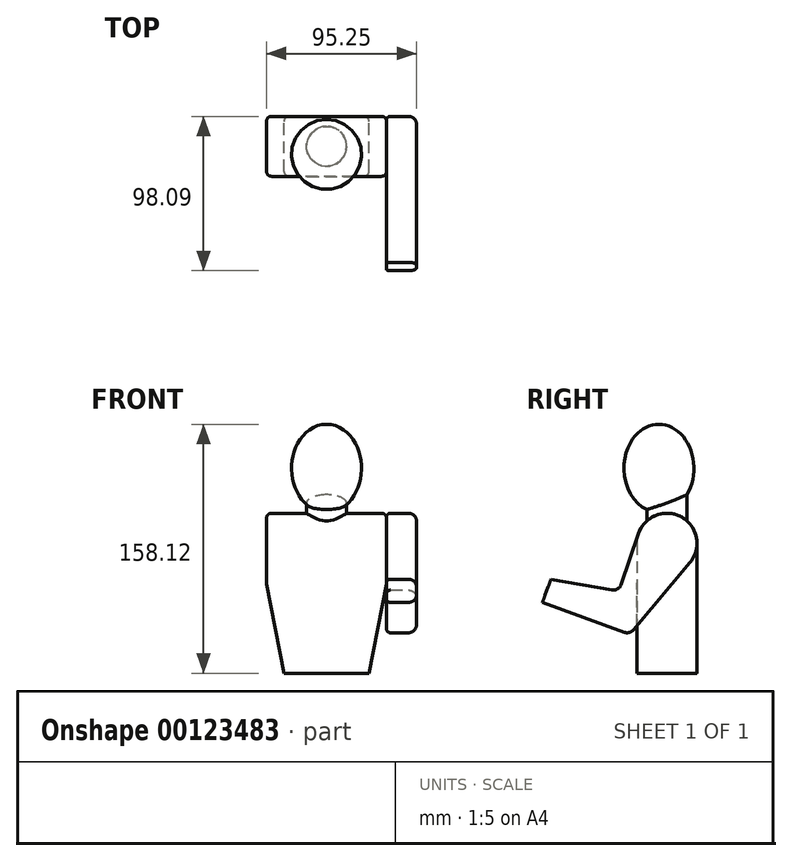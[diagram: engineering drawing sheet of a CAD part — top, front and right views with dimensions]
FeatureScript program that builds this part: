
annotation { "Feature Type Name" : "Feature", "Feature Type Description" : "" }
export const myFeature = defineFeature(function(context is Context, id is Id, definition is map)
    precondition{}
    {
        {
            var Q0;
            Q0=qCreatedBy(makeId("Front.planeOp"),FACE);
            var sketch = newSketch(context, id + "F0", { "sketchPlane" : qUnion([Q0])});
            skLineSegment(sketch, "E0", {"start": v(-26.99, 0) * mm, "end": v(26.99, 0) * mm});
            skLineSegment(sketch, "E1", {"start": v(26.99, 0) * mm, "end": v(38.1, 57.15) * mm});
            skLineSegment(sketch, "E2", {"start": v(38.1, 57.15) * mm, "end": v(38.1, 101.6) * mm});
            skLineSegment(sketch, "E3", {"start": v(38.1, 101.6) * mm, "end": v(-38.1, 101.6) * mm});
            skLineSegment(sketch, "E4", {"start": v(-38.1, 101.6) * mm, "end": v(-38.1, 57.15) * mm});
            skLineSegment(sketch, "E5", {"start": v(-38.1, 57.15) * mm, "end": v(-26.99, 0) * mm});
            skLineSegment(sketch, "E6", {"start": v(0, 0) * mm, "end": v(0, 101.6) * mm, "construction": true});
            skSolve(sketch);
        }
        {
            var Q0;
            Q0=qSketchRegion(id+"F0",true);
            extrude(context, id + "F1", {"entities" : qUnion([Q0]), "endBound" : BoundingType.SYMMETRIC, "depth" : 38.1 * mm});
        }
        {
            var Q0;
            Q0=makeQuery(id+"F1.opExtrude","CAP_EDGE",EDGE,{"disambiguationData":[OSD([sQuery(id+"F0.wireOp",EDGE,"E3")])],"isStart":false});
            var Q1;
            Q1=makeQuery(id+"F1.opExtrude","CAP_EDGE",EDGE,{"disambiguationData":[OSD([sQuery(id+"F0.wireOp",EDGE,"E3")])],"isStart":true});
            fillet(context, id + "F2", {"entities" : qUnion([Q0, Q1]), "radius" : 19.05 * mm, "tangentPropagation" : true, "allowEdgeOverflow" : false});
        }
        {
            var Q0;
            Q0=qCreatedBy(makeId("Front.planeOp"),FACE);
            var sketch = newSketch(context, id + "F3", { "sketchPlane" : qUnion([Q0])});
            skLineSegment(sketch, "E7.bottom", {"start": v(0, 82.55) * mm, "end": v(12.7, 82.55) * mm});
            skLineSegment(sketch, "E7.top", {"start": v(0, 120.65) * mm, "end": v(12.7, 120.65) * mm});
            skLineSegment(sketch, "E7.left", {"start": v(0, 82.55) * mm, "end": v(0, 120.65) * mm});
            skLineSegment(sketch, "E7.right", {"start": v(12.7, 82.55) * mm, "end": v(12.7, 120.65) * mm});
            skLineSegment(sketch, "E8", {"start": v(0, 82.55) * mm, "end": v(0, 0) * mm, "construction": true});
            skSolve(sketch);
        }
        {
            var Q0;
            Q0=qSketchRegion(id+"F3",true);
            var Q1;
            Q1=sQuery(id+"F3.wireOp",EDGE,"E8");
            revolve(context, id + "F4", {"operationType" : NewBodyOperationType.ADD, "entities" : qUnion([Q0]), "axis" : qUnion([Q1]), "revolveType" : RevolveType.FULL});
        }
        {
            var Q0;
            Q0=qCreatedBy(makeId("Right.planeOp"),FACE);
            var sketch = newSketch(context, id + "F5", { "sketchPlane" : qUnion([Q0])});
            skLineSegment(sketch, "E9", {"start": v(-5.08, 102.24) * mm, "end": v(-5.08, 158.12) * mm});
            skEllipticalArc(sketch, "E10", {});
            skLineSegment(sketch, "E11", {"start": v(-5.08, 102.24) * mm, "end": v(-5.08, 8.32) * mm, "construction": true});
            skLineSegment(sketch, "E12", {"start": v(-5.08, 130.18) * mm, "end": v(17.14, 130.18) * mm, "construction": true});
            const initialGuessF5  = {"E10": [-0.00508, 0.130175, 0, 1, 0.02794, 0.022225, 3.141592653589793, 0]};
            skSetInitialGuess(sketch, initialGuessF5);
            skSolve(sketch);
        }
        {
            var Q0;
            Q0=qSketchRegion(id+"F5",true);
            var Q1;
            Q1=sQuery(id+"F5.wireOp",EDGE,"E11");
            revolve(context, id + "F6", {"operationType" : NewBodyOperationType.ADD, "entities" : qUnion([Q0]), "axis" : qUnion([Q1]), "revolveType" : RevolveType.FULL});
        }
        {
            var Q0;
            Q0=makeQuery(id+"F1.opExtrude","SWEPT_EDGE",EDGE,{"disambiguationData":[OSD([sQuery(id+"F0.wireOp",EDGE,"E4"),sQuery(id+"F0.wireOp",EDGE,"E5")])]});
            var Q1;
            Q1=makeQuery(id+"F1.opExtrude","SWEPT_EDGE",EDGE,{"disambiguationData":[OSD([sQuery(id+"F0.wireOp",EDGE,"E1"),sQuery(id+"F0.wireOp",EDGE,"E2")])]});
            fillet(context, id + "F7", {"entities" : qUnion([Q0, Q1]), "radius" : 3.17 * mm, "tangentPropagation" : true, "allowEdgeOverflow" : false});
        }
        {
            var Q0;
            Q0=makeQuery(id+"F1.opExtrude","CAP_EDGE",EDGE,{"disambiguationData":[OSD([sQuery(id+"F0.wireOp",EDGE,"E1")])],"isStart":false});
            var Q1;
            Q1=makeQuery(id+"F1.opExtrude","CAP_EDGE",EDGE,{"disambiguationData":[OSD([sQuery(id+"F0.wireOp",EDGE,"E5")])],"isStart":false});
            fillet(context, id + "F8", {"entities" : qUnion([Q0, Q1]), "radius" : 3.17 * mm, "tangentPropagation" : true, "allowEdgeOverflow" : false});
        }
        {
            var Q0;
            Q0=makeQuery(id+"F1.opExtrude","SWEPT_FACE",FACE,{"disambiguationData":[OSD([sQuery(id+"F0.wireOp",EDGE,"E2")])]});
            var sketch = newSketch(context, id + "F9", { "sketchPlane" : qUnion([Q0])});
            skLineSegment(sketch, "E13", {"start": v(14.6, 70.3) * mm, "end": v(-23.62, 24.76) * mm});
            skLineSegment(sketch, "E14", {"start": v(-23.62, 24.76) * mm, "end": v(-79.04, 44.93) * mm});
            skLineSegment(sketch, "E15", {"start": v(-79.04, 44.93) * mm, "end": v(-73.66, 59.7) * mm});
            skLineSegment(sketch, "E16", {"start": v(-73.66, 59.7) * mm, "end": v(-30.48, 52.08) * mm});
            skLineSegment(sketch, "E17", {"start": v(-30.48, 52.08) * mm, "end": v(-18.04, 88.68) * mm});
            skArc(sketch, "E18.0", {"start": v(-18.04, 88.68) * mm, "mid": v(9.35, 99.15) * mm, "end": v(14.6, 70.3) * mm});
            skPoint(sketch, "E19.orphan", {"position": v(-19.05, 82.55) * mm});
            skPoint(sketch, "E20.orphan", {"position": v(19.05, 82.55) * mm});
            skSolve(sketch);
        }
        {
            var Q0;
            Q0=qSketchRegion(id+"F9",true);
            extrude(context, id + "F10", {"entities" : qUnion([Q0]), "depth" : 19.05 * mm});
        }
        {
            var Q0;
            Q0=makeQuery(id+"F10.opExtrude","SWEPT_EDGE",EDGE,{"disambiguationData":[OSD([sQuery(id+"F9.wireOp",EDGE,"E16"),sQuery(id+"F9.wireOp",EDGE,"E17")])]});
            var Q1;
            Q1=makeQuery(id+"FG809VM8ehI65F2_1.1.F10.opExtrude","SWEPT_EDGE",EDGE,{"disambiguationData":[OSD([sQuery(id+"F9.wireOp",EDGE,"E16"),sQuery(id+"F9.wireOp",EDGE,"E17")])]});
            fillet(context, id + "F11", {"entities" : qUnion([Q0, Q1]), "radius" : 5.08 * mm, "tangentPropagation" : true, "allowEdgeOverflow" : false});
        }
        {
            var Q0;
            Q0=makeQuery(id+"F10.opExtrude","SWEPT_EDGE",EDGE,{"disambiguationData":[OSD([sQuery(id+"F9.wireOp",EDGE,"E13"),sQuery(id+"F9.wireOp",EDGE,"E14")])]});
            var Q1;
            Q1=makeQuery(id+"FG809VM8ehI65F2_1.1.F10.opExtrude","SWEPT_EDGE",EDGE,{"disambiguationData":[OSD([sQuery(id+"F9.wireOp",EDGE,"E13"),sQuery(id+"F9.wireOp",EDGE,"E14")])]});
            fillet(context, id + "F12", {"entities" : qUnion([Q0, Q1]), "radius" : 5.08 * mm, "tangentPropagation" : true, "allowEdgeOverflow" : false});
        }
        {
            var Q0;
            Q0=makeQuery(id+"F10.opExtrude","CAP_EDGE",EDGE,{"disambiguationData":[OSD([sQuery(id+"F9.wireOp",EDGE,"E13")])],"isStart":false});
            var Q1;
            Q1=makeQuery(id+"FG809VM8ehI65F2_1.1.F10.opExtrude","CAP_EDGE",EDGE,{"disambiguationData":[OSD([sQuery(id+"F9.wireOp",EDGE,"E13")])],"isStart":false});
            fillet(context, id + "F13", {"entities" : qUnion([Q0, Q1]), "radius" : 5.08 * mm, "tangentPropagation" : true, "allowEdgeOverflow" : false});
        }
        {
            var Q0;
            Q0=makeQuery(id+"FG809VM8ehI65F2_1.1.F10.opExtrude","CAP_EDGE",EDGE,{"disambiguationData":[OSD([sQuery(id+"F9.wireOp",EDGE,"E14")])],"isStart":true});
            var Q1;
            Q1=makeQuery(id+"FG809VM8ehI65F2_1.1.F10.opExtrude","CAP_EDGE",EDGE,{"disambiguationData":[OSD([sQuery(id+"F9.wireOp",EDGE,"E16")])],"isStart":true});
            var Q2;
            {var subQ0=sQuery(id+"F9.wireOp",EDGE,"E17");var subQ1=sQuery(id+"F9.wireOp",EDGE,"E16");Q2=makeQuery(id+"F11.opFillet","BLEND_EDGE",EDGE,{"blendedFrom":[makeQuery(id+"FG809VM8ehI65F2_1.1.F10.opExtrude","SWEPT_EDGE",EDGE,{"disambiguationData":[OSD([subQ1,subQ0])]}),makeQuery(id+"FG809VM8ehI65F2_1.1.F10.opExtrude","CAP_FACE",FACE,{"disambiguationData":[OSD([sQuery(id+"F9.wireOp",EDGE,"E13"),sQuery(id+"F9.wireOp",EDGE,"E14"),sQuery(id+"F9.wireOp",EDGE,"E15"),subQ1,subQ0,sQuery(id+"F9.wireOp",EDGE,"E18.0")])],"isStart":true})],"blendedInto":[makeQuery(id+"FG809VM8ehI65F2_1.1.F10.opExtrude","CAP_FACE",FACE,{"disambiguationData":[OSD([sQuery(id+"F9.wireOp",EDGE,"E13"),sQuery(id+"F9.wireOp",EDGE,"E14"),sQuery(id+"F9.wireOp",EDGE,"E15"),subQ1,subQ0,sQuery(id+"F9.wireOp",EDGE,"E18.0")])],"isStart":true})]});}
            var Q3;
            Q3=makeQuery(id+"FG809VM8ehI65F2_1.1.F10.opExtrude","CAP_EDGE",EDGE,{"disambiguationData":[OSD([sQuery(id+"F9.wireOp",EDGE,"E17")])],"isStart":true});
            var Q4;
            {var subQ0=sQuery(id+"F9.wireOp",EDGE,"E17");var subQ2=sQuery(id+"F9.wireOp",EDGE,"E18.0");Q4=makeQuery(id+"FG809VM8ehI65F2_1.1.F10.boolean.opBoolean","SPLIT",EDGE,{"disambiguationData":[TD([makeQuery(id+"FG809VM8ehI65F2_1.1.F10.opExtrude","SWEPT_FACE",FACE,{"disambiguationData":[OSD([subQ0])]})])],"derivedFrom":makeQuery(id+"FG809VM8ehI65F2_1.1.F10.opExtrude","CAP_EDGE",EDGE,{"disambiguationData":[OSD([subQ2])],"isStart":true})});}
            var Q5;
            {var subQ0=sQuery(id+"F9.wireOp",EDGE,"E13");var subQ1=sQuery(id+"F9.wireOp",EDGE,"E14");Q5=makeQuery(id+"FG809VM8ehI65F2_1.1.F10.boolean.opBoolean","SPLIT",EDGE,{"disambiguationData":[TD([makeQuery(id+"FG809VM8ehI65F2_1.1.F10.opExtrude","SWEPT_FACE",FACE,{"disambiguationData":[OSD([subQ1])]})])],"derivedFrom":makeQuery(id+"FG809VM8ehI65F2_1.1.F10.opExtrude","CAP_EDGE",EDGE,{"disambiguationData":[OSD([subQ0])],"isStart":true})});}
            var Q6;
            {var subQ0=sQuery(id+"F9.wireOp",EDGE,"E14");var subQ1=sQuery(id+"F9.wireOp",EDGE,"E13");Q6=makeQuery(id+"F12.opFillet","BLEND_EDGE",EDGE,{"blendedFrom":[makeQuery(id+"FG809VM8ehI65F2_1.1.F10.opExtrude","SWEPT_EDGE",EDGE,{"disambiguationData":[OSD([subQ1,subQ0])]}),makeQuery(id+"FG809VM8ehI65F2_1.1.F10.opExtrude","CAP_FACE",FACE,{"disambiguationData":[OSD([subQ1,subQ0,sQuery(id+"F9.wireOp",EDGE,"E15"),sQuery(id+"F9.wireOp",EDGE,"E16"),sQuery(id+"F9.wireOp",EDGE,"E17"),sQuery(id+"F9.wireOp",EDGE,"E18.0")])],"isStart":true})],"blendedInto":[makeQuery(id+"FG809VM8ehI65F2_1.1.F10.opExtrude","CAP_FACE",FACE,{"disambiguationData":[OSD([subQ1,subQ0,sQuery(id+"F9.wireOp",EDGE,"E15"),sQuery(id+"F9.wireOp",EDGE,"E16"),sQuery(id+"F9.wireOp",EDGE,"E17"),sQuery(id+"F9.wireOp",EDGE,"E18.0")])],"isStart":true})]});}
            var Q7;
            Q7=makeQuery(id+"F10.opExtrude","CAP_EDGE",EDGE,{"disambiguationData":[OSD([sQuery(id+"F9.wireOp",EDGE,"E13")])],"isStart":true});
            fillet(context, id + "F14", {"entities" : qUnion([Q0, Q1, Q2, Q3, Q4, Q5, Q6, Q7]), "radius" : 2.54 * mm, "tangentPropagation" : true, "allowEdgeOverflow" : false});
        }
    });
